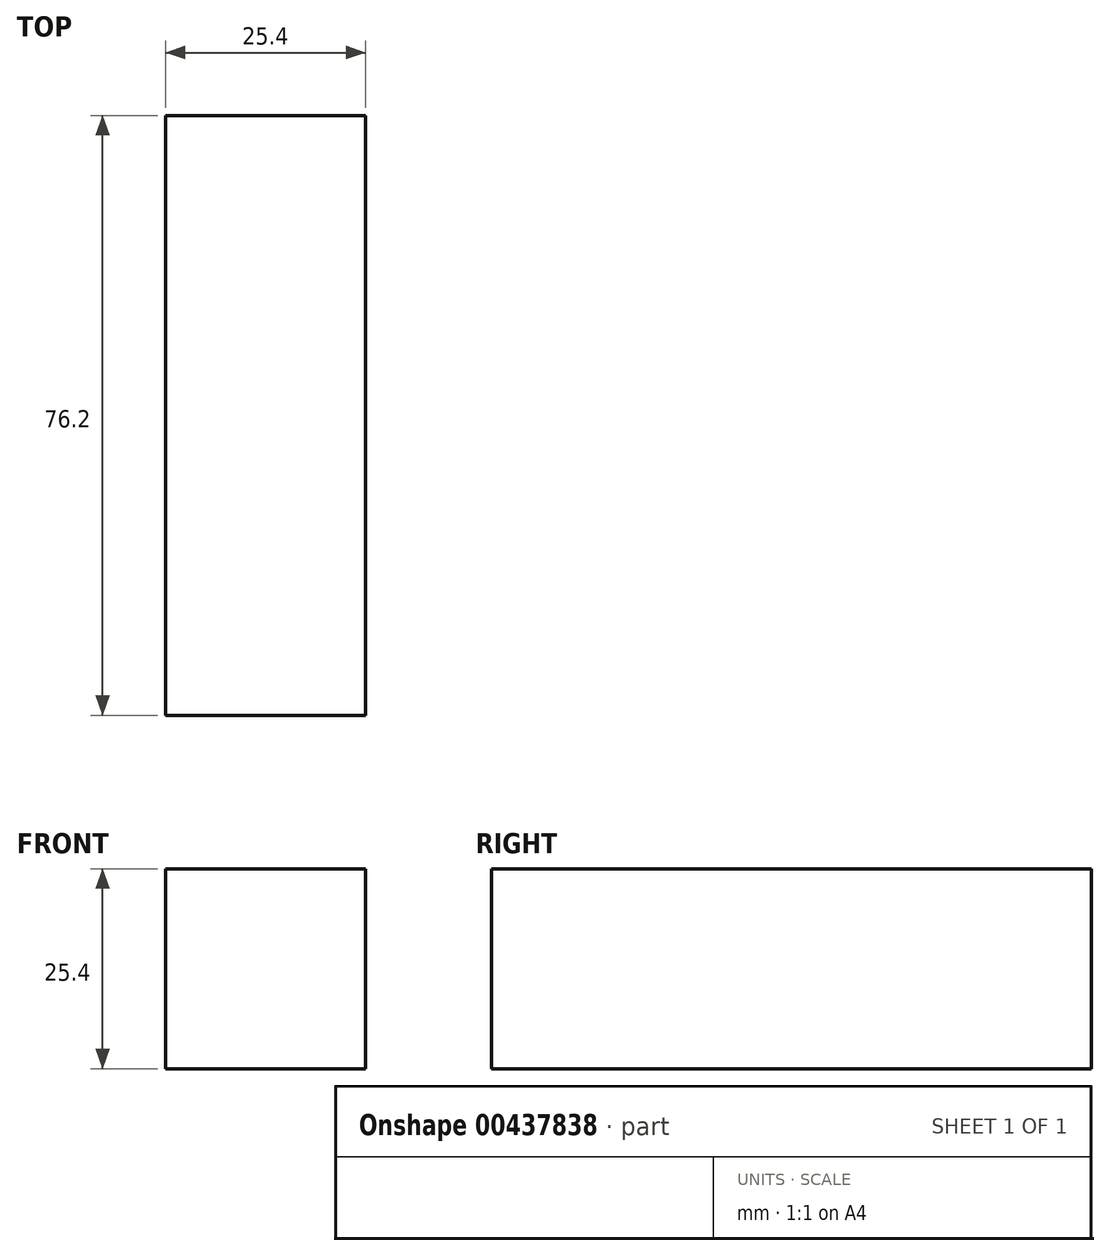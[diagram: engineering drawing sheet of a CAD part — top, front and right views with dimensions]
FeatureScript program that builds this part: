
annotation { "Feature Type Name" : "Feature", "Feature Type Description" : "" }
export const myFeature = defineFeature(function(context is Context, id is Id, definition is map)
    precondition{}
    {
        {
            var Q0;
            Q0=qCreatedBy(makeId("Front.planeOp"),FACE);
            var sketch = newSketch(context, id + "F0", { "sketchPlane" : qUnion([Q0])});
            skLineSegment(sketch, "E0", {"start": v(0, 0) * mm, "end": v(25.4, 0) * mm});
            skLineSegment(sketch, "E1", {"start": v(25.4, 0) * mm, "end": v(25.4, 25.4) * mm});
            skLineSegment(sketch, "E2", {"start": v(25.4, 25.4) * mm, "end": v(0, 25.4) * mm});
            skLineSegment(sketch, "E3", {"start": v(0, 25.4) * mm, "end": v(0, 0) * mm});
            skSolve(sketch);
        }
        {
            var Q0;
            Q0 = qSketchRegion(id + "F0", true);
            extrude(context, id + "F1", {"entities" : qUnion([Q0]), "depth" : 76.2 * mm});
        }
    });
